# Revit family: ledroadlight-200w-4000-step_543014015800
name_source: partatom
category: Leuchten
revit_build: Autodesk Revit 2016 (Build: 20190508_0715(x64)
units: mm (PartAtom-declared; Revit-internal decimal feet)

## family parameters
Basisbauteil = Fläche
Beim Laden mit Abzugskörper schneiden = Nein
Bemaßung runder Anschluss = Durchmesser verwenden
Gemeinsam genutzt = Nein
Lichtquelle = Nein
Raumberechnungspunkt = Nein
Teiletyp = Normal

## types (1)
- LEDRoadlight-200W-4000-STEP (1 x LED, 24000 lm)
    Approval mark = CE, ENEC
    Beschreibung = Modern-looking Roadlight solution with robust die-cast aluminium body. Up to 60% energy saving compared to HID roadlights
. Advanced optical design optimized for road lighting. Flexible and adjustable pole connector for both side entry and pole top mounting. IP66 and suitable for use on the coastal applications. Including 10m H07RN-F rubber cable 5x1,5mm² pre-assembled for faster installation. Double pole-top adapter available as accessory.
    CIE Flux Codes = 45 80 99 100 100
    Control Gear = Electronic ballast
    Height = 112 mm
    Hersteller = OPPLE
    Lamp Light Flux = 24000 lm
    Lamp count = 1
    Lampe = 1 x LED
    Length = 645 mm
    Luminous efficacy = 120 lm/W
    ModVariant = Nein
    Modell = 543014015800
    Mounting Place = Pole
    Mounting Type = Pole top, Pole annexe
    Number of Poles = 1
    OnlyDefault = Ja
    Power Factor = 1
    Product Name = LEDRoadlight-200W-4000-STEP
    Product group = Roadlight
    ProductGroupID = 6220
    Protection Class = Protection class I
    Protection Degree = IP 66
    RLX_Detail_Level = 1
    RlxData = <blob elided: 183937 chars, md5=f2d125fa>
    Scheinlast = 200 VA
    Socket = socket
    Standby Power = 0 W
    System Light Flux = 24000 lm
    System Power = 200 W
    Typenbild = 543014015800.jpg
    Typenkommentare = Product without accessories
    URL = http://relux.com
    VarID = ---
    Voltage = 0 V
    Vorgabe-Ansicht = 1800 mm
    Weight = 0.00 kg
    Width = 310 mm

## geometry (parser evidence)
native form markers: Blend x4, Sweep x10
no freeform markers — native parametric forms only
